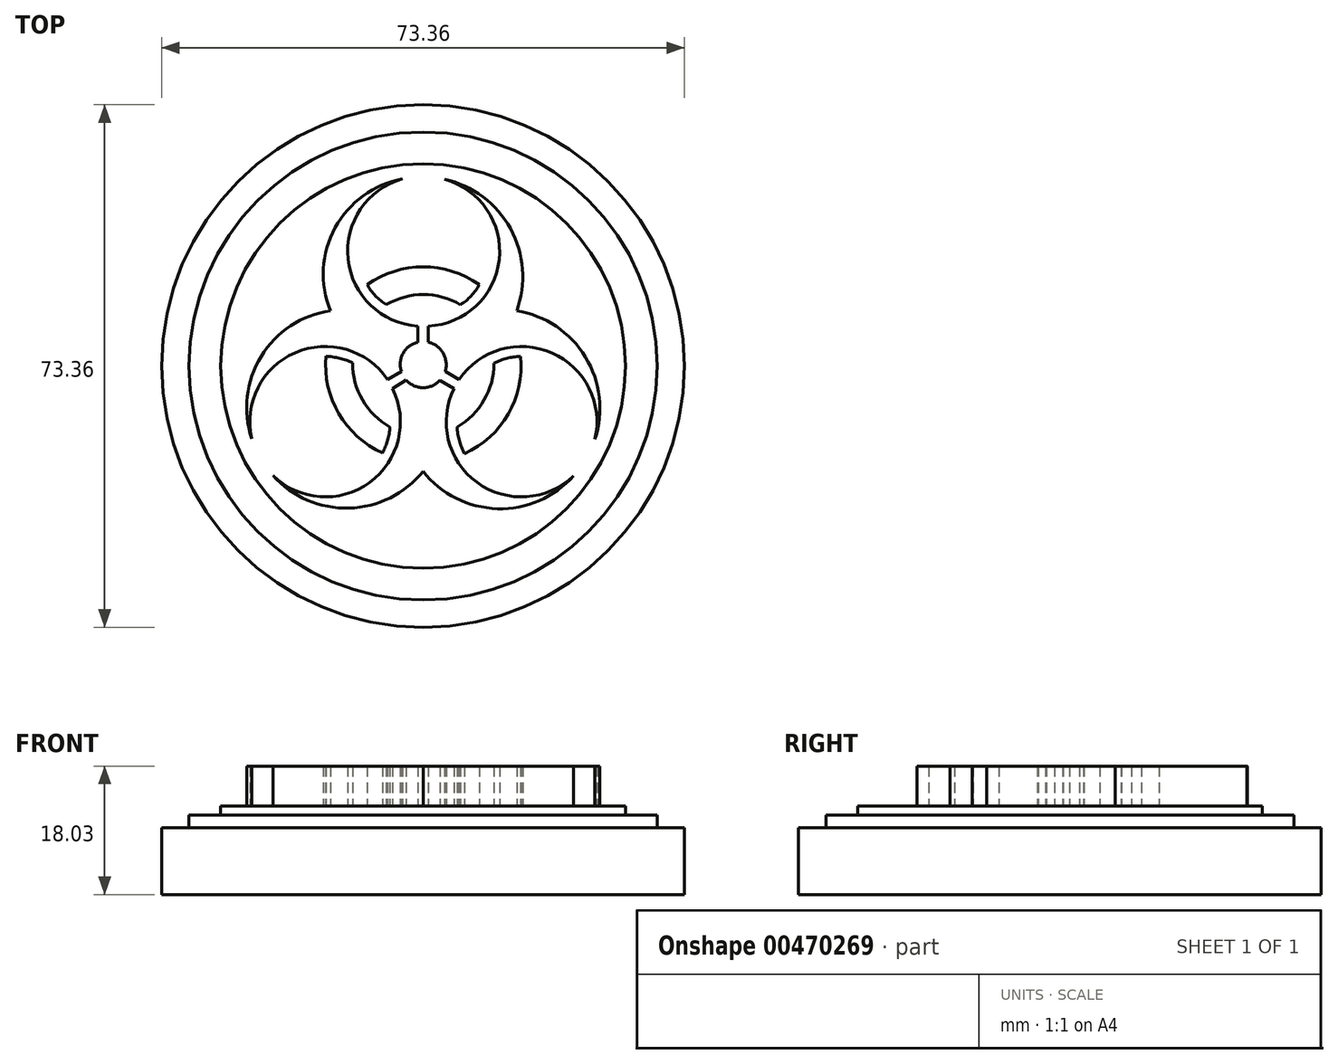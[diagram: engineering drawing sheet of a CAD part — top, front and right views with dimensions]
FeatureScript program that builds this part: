
annotation { "Feature Type Name" : "Feature", "Feature Type Description" : "" }
export const myFeature = defineFeature(function(context is Context, id is Id, definition is map)
    precondition{}
    {
        {
            var Q0;
            Q0=qCreatedBy(makeId("Top.planeOp"),FACE);
            var sketch = newSketch(context, id + "F0", { "sketchPlane" : qUnion([Q0])});
            skArc(sketch, "E0", {"start": v(-0.72, 3.32) * mm, "mid": v(-2.8, 1.8) * mm, "end": v(-3.03, -0.77) * mm});
            skArc(sketch, "E1", {"start": v(3.13, -0.75) * mm, "mid": v(2.8, 1.8) * mm, "end": v(0.75, 3.36) * mm});
            skArc(sketch, "E2", {"start": v(-2.36, -2) * mm, "mid": v(0, -3.05) * mm, "end": v(2.38, -2) * mm});
            skLineSegment(sketch, "E3", {"start": v(-3.03, -0.77) * mm, "end": v(-4.97, -1.9) * mm});
            skLineSegment(sketch, "E4", {"start": v(-2.36, -2) * mm, "end": v(-4.29, -3.17) * mm});
            skLineSegment(sketch, "E5", {"start": v(2.38, -2) * mm, "end": v(4.34, -3.15) * mm});
            skLineSegment(sketch, "E6", {"start": v(4.34, -3.15) * mm, "end": v(2.38, -2) * mm});
            skLineSegment(sketch, "E7", {"start": v(3.13, -0.75) * mm, "end": v(5.06, -1.88) * mm});
            skLineSegment(sketch, "E8", {"start": v(5.06, -1.88) * mm, "end": v(3.13, -0.75) * mm});
            skLineSegment(sketch, "E9", {"start": v(-0.72, 3.32) * mm, "end": v(-0.72, 5.6) * mm});
            skLineSegment(sketch, "E10", {"start": v(-0.72, 5.6) * mm, "end": v(-0.72, 3.32) * mm});
            skLineSegment(sketch, "E11", {"start": v(0.75, 3.36) * mm, "end": v(0.75, 5.6) * mm});
            skLineSegment(sketch, "E12", {"start": v(0.75, 5.6) * mm, "end": v(0.75, 3.36) * mm});
            skArc(sketch, "E13", {"start": v(0.75, 5.6) * mm, "mid": v(10.68, 14.94) * mm, "end": v(3.02, 26.21) * mm});
            skArc(sketch, "E14", {"start": v(-2.9, 26.27) * mm, "mid": v(-10.53, 15.01) * mm, "end": v(-0.72, 5.6) * mm});
            skArc(sketch, "E15", {"start": v(24.11, -10.3) * mm, "mid": v(18.09, 1.83) * mm, "end": v(5.06, -1.88) * mm});
            skArc(sketch, "E16", {"start": v(4.34, -3.15) * mm, "mid": v(7.57, -16.35) * mm, "end": v(21.13, -15.42) * mm});
            skArc(sketch, "E17", {"start": v(-21.07, -15.39) * mm, "mid": v(-7.52, -16.37) * mm, "end": v(-4.29, -3.17) * mm});
            skArc(sketch, "E18", {"start": v(-4.97, -1.9) * mm, "mid": v(-17.96, 1.86) * mm, "end": v(-24.04, -10.21) * mm});
            skArc(sketch, "E19", {"start": v(-21.07, -15.39) * mm, "mid": v(-10.4, -19.96) * mm, "end": v(0, -14.78) * mm});
            skArc(sketch, "E20", {"start": v(0, -14.78) * mm, "mid": v(10.41, -20.04) * mm, "end": v(21.13, -15.42) * mm});
            skArc(sketch, "E21", {"start": v(24.11, -10.3) * mm, "mid": v(22.79, 1.25) * mm, "end": v(13.14, 7.75) * mm});
            skArc(sketch, "E22", {"start": v(13.14, 7.75) * mm, "mid": v(12.27, 19.28) * mm, "end": v(3.02, 26.21) * mm});
            skArc(sketch, "E23", {"start": v(-2.9, 26.27) * mm, "mid": v(-12.34, 19.4) * mm, "end": v(-13, 7.75) * mm});
            skArc(sketch, "E24", {"start": v(-13, 7.75) * mm, "mid": v(-22.73, 1.36) * mm, "end": v(-24.04, -10.21) * mm});
            skArc(sketch, "E25", {"start": v(-9.9, 0.45) * mm, "mid": v(-8.5, -4.76) * mm, "end": v(-4.66, -8.55) * mm});
            skArc(sketch, "E26", {"start": v(-13.62, 1.37) * mm, "mid": v(-11.84, -6.7) * mm, "end": v(-5.68, -12.2) * mm});
            skArc(sketch, "E27", {"start": v(-9.9, 0.45) * mm, "mid": v(-11.72, 1.08) * mm, "end": v(-13.62, 1.37) * mm});
            skArc(sketch, "E28", {"start": v(-5.68, -12.2) * mm, "mid": v(-4.97, -10.43) * mm, "end": v(-4.66, -8.55) * mm});
            skArc(sketch, "E29", {"start": v(5.82, -12.3) * mm, "mid": v(11.95, -6.76) * mm, "end": v(13.66, 1.32) * mm});
            skArc(sketch, "E30", {"start": v(4.78, -8.56) * mm, "mid": v(8.56, -4.79) * mm, "end": v(9.96, 0.36) * mm});
            skArc(sketch, "E31", {"start": v(13.66, 1.32) * mm, "mid": v(11.74, 1.08) * mm, "end": v(9.96, 0.36) * mm});
            skArc(sketch, "E32", {"start": v(4.78, -8.56) * mm, "mid": v(5.08, -10.49) * mm, "end": v(5.82, -12.3) * mm});
            skArc(sketch, "E33", {"start": v(5.24, 8.6) * mm, "mid": v(0.04, 10.02) * mm, "end": v(-5.16, 8.62) * mm});
            skArc(sketch, "E34", {"start": v(7.88, 11.42) * mm, "mid": v(0.01, 13.92) * mm, "end": v(-7.85, 11.42) * mm});
            skArc(sketch, "E35", {"start": v(5.24, 8.6) * mm, "mid": v(6.74, 9.84) * mm, "end": v(7.88, 11.42) * mm});
            skArc(sketch, "E36", {"start": v(-7.85, 11.42) * mm, "mid": v(-6.69, 9.85) * mm, "end": v(-5.16, 8.62) * mm});
            skCircle(sketch, "E37", {"center": v(0, 0) * mm, "radius": 28.4 * mm});
            skCircle(sketch, "E38", {"center": v(0, 0) * mm, "radius": 32.85 * mm});
            skCircle(sketch, "E39", {"center": v(0, 0) * mm, "radius": 36.68 * mm});
            skSolve(sketch);
        }
        {
            var Q0;
            Q0=makeQuery(id+"F0.imprint","IMPRINT",FACE,{"disambiguationData":[TD([[makeQuery(id+"F0.imprint","IMPRINT",EDGE,{"derivedFrom":sQuery(id+"F0.wireOp",EDGE,"E0")}),1.0]])]});
            extrude(context, id + "F1", {"entities" : qUnion([Q0]), "depth" : 12.45 * mm});
        }
        {
            var Q0;
            Q0=makeQuery(id+"F0.imprint","IMPRINT",FACE,{"disambiguationData":[TD([[makeQuery(id+"F0.imprint","IMPRINT",EDGE,{"derivedFrom":sQuery(id+"F0.wireOp",EDGE,"E37")}),-1.0]])]});
            extrude(context, id + "F2", {"entities" : qUnion([Q0]), "operationType" : NewBodyOperationType.ADD, "depth" : 11.18 * mm});
        }
        {
            var Q0;
            Q0=makeQuery(id+"F0.imprint","IMPRINT",FACE,{"disambiguationData":[TD([[makeQuery(id+"F0.imprint","IMPRINT",EDGE,{"derivedFrom":sQuery(id+"F0.wireOp",EDGE,"E38")}),-1.0]])]});
            extrude(context, id + "F3", {"entities" : qUnion([Q0]), "operationType" : NewBodyOperationType.ADD, "depth" : 9.4 * mm});
        }
        {
            var Q0;
            Q0=makeQuery(id+"F0.imprint","IMPRINT",FACE,{"disambiguationData":[TD([[makeQuery(id+"F0.imprint","IMPRINT",EDGE,{"derivedFrom":sQuery(id+"F0.wireOp",EDGE,"E0")}),-1.0]])]});
            var Q1;
            Q1=makeQuery(id+"F0.imprint","IMPRINT",FACE,{"disambiguationData":[TD([[makeQuery(id+"F0.imprint","IMPRINT",EDGE,{"derivedFrom":sQuery(id+"F0.wireOp",EDGE,"E1")}),-1.0]])]});
            var Q2;
            Q2=makeQuery(id+"F0.imprint","IMPRINT",FACE,{"disambiguationData":[TD([[makeQuery(id+"F0.imprint","IMPRINT",EDGE,{"derivedFrom":sQuery(id+"F0.wireOp",EDGE,"E2")}),-1.0]])]});
            var Q3;
            Q3=makeQuery(id+"F0.imprint","IMPRINT",FACE,{"disambiguationData":[TD([[makeQuery(id+"F0.imprint","IMPRINT",EDGE,{"derivedFrom":sQuery(id+"F0.wireOp",EDGE,"E25")}),-1.0]])]});
            var Q4;
            Q4=makeQuery(id+"F0.imprint","IMPRINT",FACE,{"disambiguationData":[TD([[makeQuery(id+"F0.imprint","IMPRINT",EDGE,{"derivedFrom":sQuery(id+"F0.wireOp",EDGE,"E33")}),-1.0]])]});
            var Q5;
            Q5=makeQuery(id+"F0.imprint","IMPRINT",FACE,{"disambiguationData":[TD([[makeQuery(id+"F0.imprint","IMPRINT",EDGE,{"derivedFrom":sQuery(id+"F0.wireOp",EDGE,"E29")}),1.0]])]});
            extrude(context, id + "F4", {"entities" : qUnion([Q0, Q1, Q2, Q3, Q4, Q5]), "operationType" : NewBodyOperationType.ADD, "depth" : 18.03 * mm});
        }
    });
